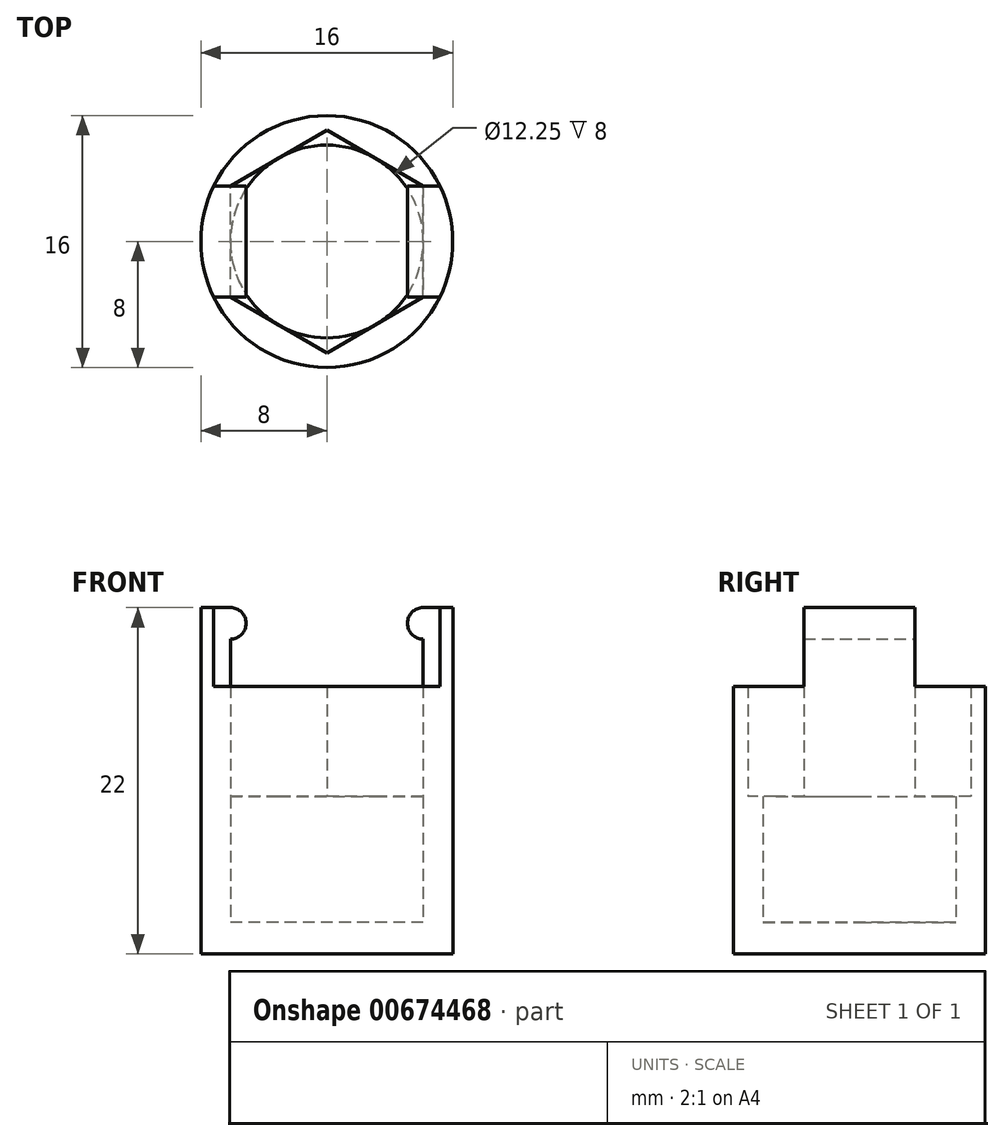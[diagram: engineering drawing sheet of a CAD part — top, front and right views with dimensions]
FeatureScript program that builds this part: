
annotation { "Feature Type Name" : "Feature", "Feature Type Description" : "" }
export const myFeature = defineFeature(function(context is Context, id is Id, definition is map)
    precondition{}
    {
        {
            var Q0;
            Q0=qCreatedBy(makeId("Top.planeOp"),FACE);
            var sketch = newSketch(context, id + "F0", { "sketchPlane" : qUnion([Q0])});
            skCircle(sketch, "E0", {"center": v(0, 0) * mm, "radius": 6.12 * mm});
            skCircle(sketch, "E1", {"center": v(0, 0) * mm, "radius": 8 * mm});
            skSolve(sketch);
        }
        {
            var Q0;
            Q0=makeQuery(id+"F0.imprint","IMPRINT",FACE,{"disambiguationData":[TD([[makeQuery(id+"F0.imprint","IMPRINT",EDGE,{"derivedFrom":sQuery(id+"F0.wireOp",EDGE,"E0")}),1.0]])]});
            extrude(context, id + "F1", {"entities" : qUnion([Q0]), "depth" : 2 * mm, "offsetDistance" : 25 * mm});
        }
        {
            var Q0;
            Q0 = qSketchRegion(id + "F0", true);
            extrude(context, id + "F2", {"entities" : qUnion([Q0]), "operationType" : NewBodyOperationType.ADD, "depth" : 10 * mm, "offsetDistance" : 25 * mm});
        }
        {
            var Q0;
            Q0=makeQuery(id+"F2.opExtrude","CAP_FACE",FACE,{"disambiguationData":[OSD([sQuery(id+"F0.wireOp",EDGE,"E0"),sQuery(id+"F0.wireOp",EDGE,"E1")])],"isStart":false});
            var sketch = newSketch(context, id + "F3", { "sketchPlane" : qUnion([Q0])});
            skCircle(sketch, "E2.cCircle", {"center": v(0, 0) * mm, "radius": 6.12 * mm, "construction": true});
            skLineSegment(sketch, "E2.0", {"start": v(6.12, 3.54) * mm, "end": v(6.12, -3.54) * mm});
            skLineSegment(sketch, "E2.1", {"start": v(6.13, -3.54) * mm, "end": v(0, -7.07) * mm});
            skLineSegment(sketch, "E2.2", {"start": v(0, -7.07) * mm, "end": v(-6.13, -3.54) * mm});
            skLineSegment(sketch, "E2.3", {"start": v(-6.12, -3.54) * mm, "end": v(-6.12, 3.54) * mm});
            skLineSegment(sketch, "E2.4", {"start": v(-6.12, 3.54) * mm, "end": v(0, 7.07) * mm});
            skLineSegment(sketch, "E2.5", {"start": v(0, 7.07) * mm, "end": v(6.13, 3.54) * mm});
            skPoint(sketch, "E2.0.midPoint", {"position": v(6.12, 0) * mm});
            skSolve(sketch);
        }
        {
            var Q0;
            Q0=makeQuery(id+"F3.imprint","IMPRINT",FACE,{"disambiguationData":[TD([[makeQuery(id+"F3.imprint","IMPRINT",EDGE,{"derivedFrom":makeQuery(id+"F2.opExtrude","CAP_EDGE",EDGE,{"disambiguationData":[OSD([sQuery(id+"F0.wireOp",EDGE,"E1")])],"isStart":false})}),1.0]])]});
            extrude(context, id + "F4", {"entities" : qUnion([Q0]), "operationType" : NewBodyOperationType.ADD, "depth" : 7 * mm, "offsetDistance" : 25 * mm});
        }
        {
            var Q0;
            Q0=makeQuery(id+"F4.opExtrude","CAP_FACE",FACE,{"disambiguationData":[OSD([sQuery(id+"F0.wireOp",EDGE,"E1"),sQuery(id+"F3.wireOp",EDGE,"E2.0"),sQuery(id+"F3.wireOp",EDGE,"E2.1"),sQuery(id+"F3.wireOp",EDGE,"E2.2"),sQuery(id+"F3.wireOp",EDGE,"E2.3"),sQuery(id+"F3.wireOp",EDGE,"E2.4"),sQuery(id+"F3.wireOp",EDGE,"E2.5")])],"isStart":false});
            var sketch = newSketch(context, id + "F5", { "sketchPlane" : qUnion([Q0])});
            skLineSegment(sketch, "E3", {"start": v(-6.12, 3.54) * mm, "end": v(-7.18, 3.54) * mm});
            skLineSegment(sketch, "E4", {"start": v(-6.13, -3.54) * mm, "end": v(-7.18, -3.54) * mm});
            skLineSegment(sketch, "E5", {"start": v(6.12, -3.54) * mm, "end": v(7.18, -3.54) * mm});
            skLineSegment(sketch, "E6", {"start": v(6.12, 3.54) * mm, "end": v(7.18, 3.54) * mm});
            skSolve(sketch);
        }
        {
            var Q0;
            {var subQ0=sQuery(id+"F5.wireOp",EDGE,"E3");Q0=makeQuery(id+"F5.imprint","IMPRINT",FACE,{"disambiguationData":[TD([[makeQuery(id+"F5.imprint","IMPRINT",EDGE,{"derivedFrom":subQ0}),1.0]])]});}
            var Q1;
            {var subQ0=sQuery(id+"F5.wireOp",EDGE,"E5");Q1=makeQuery(id+"F5.imprint","IMPRINT",FACE,{"disambiguationData":[TD([[makeQuery(id+"F5.imprint","IMPRINT",EDGE,{"derivedFrom":subQ0}),1.0]])]});}
            extrude(context, id + "F6", {"entities" : qUnion([Q0, Q1]), "operationType" : NewBodyOperationType.ADD, "depth" : 5 * mm, "offsetDistance" : 25 * mm});
        }
        {
            var Q0;
            Q0=makeQuery(id+"F6.opExtrude","SWEPT_FACE",FACE,{"disambiguationData":[OSD([sQuery(id+"F5.wireOp",EDGE,"E3")])]});
            var sketch = newSketch(context, id + "F7", { "sketchPlane" : qUnion([Q0])});
            skArc(sketch, "E7", {"start": v(6.12, 22) * mm, "mid": v(5.12, 21) * mm, "end": v(6.12, 20) * mm});
            skSolve(sketch);
        }
        {
            var Q0;
            {var subQ0=sQuery(id+"F7.wireOp",EDGE,"E7");Q0=makeQuery(id+"F7.imprint","IMPRINT",FACE,{"disambiguationData":[TD([[makeQuery(id+"F7.imprint","IMPRINT",EDGE,{"derivedFrom":subQ0}),1.0]])]});}
            var Q1;
            Q1=makeQuery(id+"F6.opExtrude","SWEPT_FACE",FACE,{"disambiguationData":[OSD([sQuery(id+"F5.wireOp",EDGE,"E4")])]});
            extrude(context, id + "F8", {"entities" : qUnion([Q0]), "operationType" : NewBodyOperationType.ADD, "endBound" : BoundingType.UP_TO_SURFACE, "oppositeDirection" : true, "depth" : 25 * mm, "endBoundEntityFace" : qUnion([Q1]), "offsetDistance" : 25 * mm});
        }
        {
            var Q0;
            Q0=makeQuery(id+"F6.opExtrude","SWEPT_FACE",FACE,{"disambiguationData":[OSD([sQuery(id+"F5.wireOp",EDGE,"E6")])]});
            var sketch = newSketch(context, id + "F9", { "sketchPlane" : qUnion([Q0])});
            skArc(sketch, "E8", {"start": v(-6.12, 20) * mm, "mid": v(-5.13, 21) * mm, "end": v(-6.12, 22) * mm});
            skSolve(sketch);
        }
        {
            var Q0;
            {var subQ0=sQuery(id+"F9.wireOp",EDGE,"E8");Q0=makeQuery(id+"F9.imprint","IMPRINT",FACE,{"disambiguationData":[TD([[makeQuery(id+"F9.imprint","IMPRINT",EDGE,{"derivedFrom":subQ0}),1.0]])]});}
            var Q1;
            Q1=makeQuery(id+"F6.opExtrude","SWEPT_FACE",FACE,{"disambiguationData":[OSD([sQuery(id+"F5.wireOp",EDGE,"E5")])]});
            extrude(context, id + "F10", {"entities" : qUnion([Q0]), "operationType" : NewBodyOperationType.ADD, "endBound" : BoundingType.UP_TO_SURFACE, "oppositeDirection" : true, "depth" : 25 * mm, "endBoundEntityFace" : qUnion([Q1]), "offsetDistance" : 25 * mm});
        }
    });
